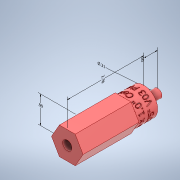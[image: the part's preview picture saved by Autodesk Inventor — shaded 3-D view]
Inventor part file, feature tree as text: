
AUTODESK INVENTOR PART (.ipt)
format: ipt  version: 2022.2 (Build 262287010, 287A)  size: 1,624,064 bytes
history: native  units: in
note: dims shown in document units (in); Inventor stores cm internally (conversion verified against a paired STEP export)
features: other x6, sketch x5, extrude x3, plane x1, emboss x1, hole x1
ambient origin geometry x8: Origin, YZ Plane, XZ Plane, XY Plane, X Axis, Y Axis, Z Axis, Center Point
bodies: Solid1 (feature_tree)
feature tree (17):
  other  "Annotations"
  extrude  "Hex Portion"  Depth=2.025in TaperAngle=0.0deg
  extrude  "Extrusion2"  Depth=0.75in TaperAngle=0.0deg
  other  "Reduce Size of Hex Shaft"
  extrude  "Extrusion3"  Depth=0.315in
  plane  "Work Plane1"
  emboss  "Emboss1"
  hole  "Hole1"  [1 undecoded]
  sketch  "Sketch1"  dims[d0=1.0in d1=2.025in d2=0.0in]
  sketch  "Sketch2"  dims[d3=1.0in d4=0.75in d5=0.0in]
  sketch  "Sketch3"  dims[d6=0.0038in d7=0.005in d14=0.315in]
  sketch  "Sketch4"  dims[d16=0.5in d17=0.0in d21=0.1in d22=0.0in]
  sketch  "Sketch5"  dims[d23=0.196in d24=0.5in d25=0.335in d26=0.5in d27=0.5635in d28=1.0in d29=0.0in d10=2.775in d11=0.2621in d12=0.2706in d13=0.9925in d18=0.5in d19=2.4445in d20=0.315in]
  other  "Linear Dimension 1"
  other  "Linear Dimension 2"
  other  "Linear Dimension 4"
  other  "Diameter Dimension 1"
note: 1 required parameter value undecoded (feature->parameter linkage not recoverable at this tier; creation-order binding heuristic only, values carry confidence <= 0.55)
